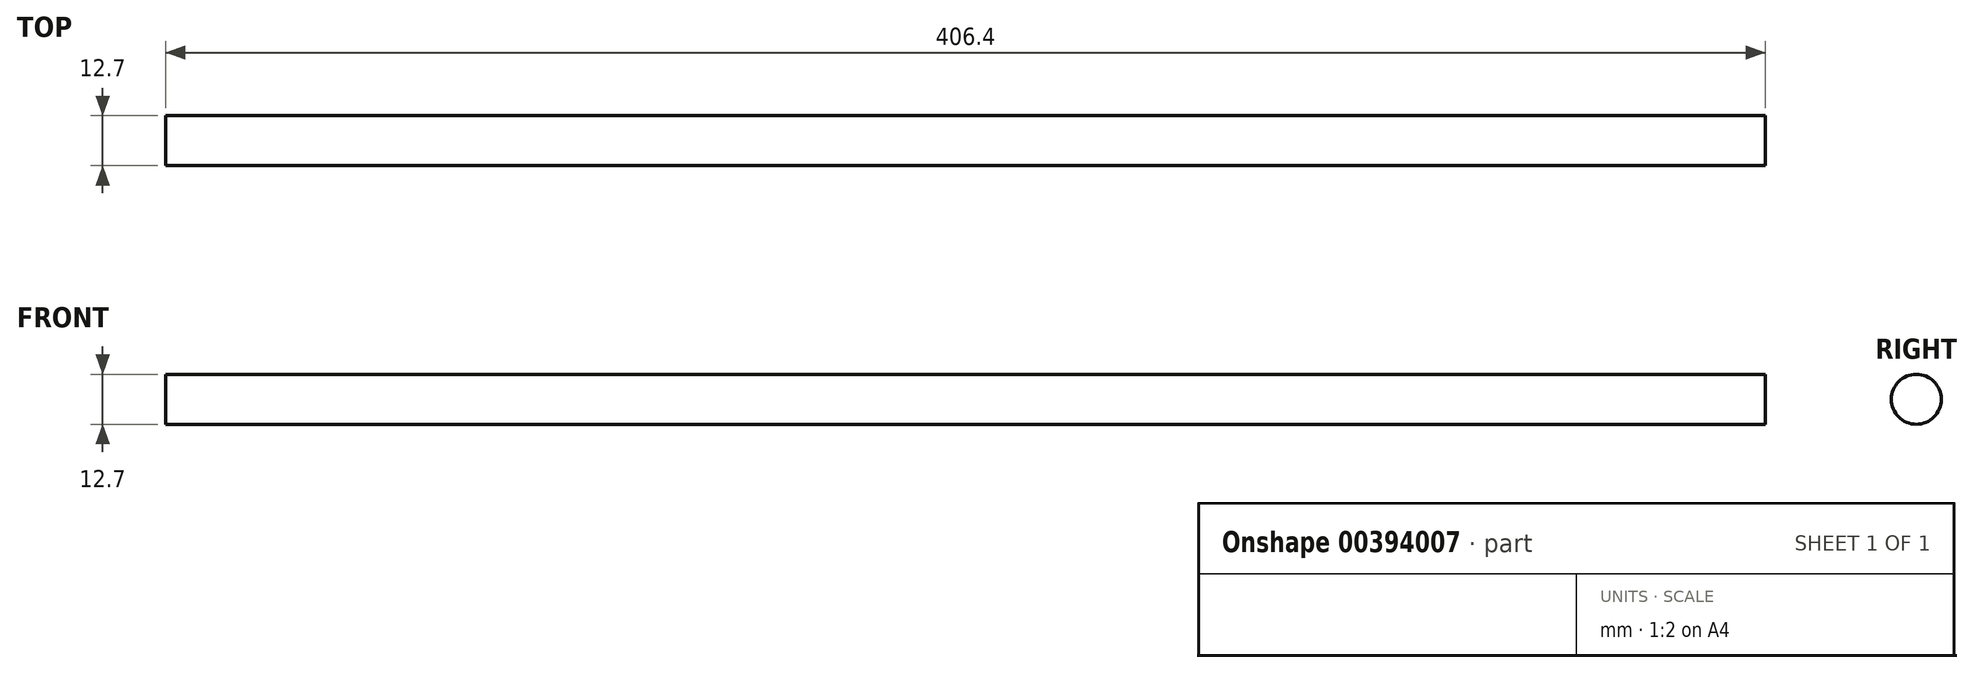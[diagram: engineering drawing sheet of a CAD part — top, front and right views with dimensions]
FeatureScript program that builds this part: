
annotation { "Feature Type Name" : "Feature", "Feature Type Description" : "" }
export const myFeature = defineFeature(function(context is Context, id is Id, definition is map)
    precondition{}
    {
        {
            var Q0;
            Q0=qCreatedBy(makeId("Right.planeOp"),FACE);
            var sketch = newSketch(context, id + "F0", { "sketchPlane" : qUnion([Q0])});
            skCircle(sketch, "E0", {"center": v(0, 0) * mm, "radius": 6.35 * mm});
            skSolve(sketch);
        }
        {
            var Q0;
            Q0=qSketchRegion(id+"F0",true);
            extrude(context, id + "F1", {"entities" : qUnion([Q0]), "oppositeDirection" : true, "depth" : 406.4 * mm});
        }
    });
